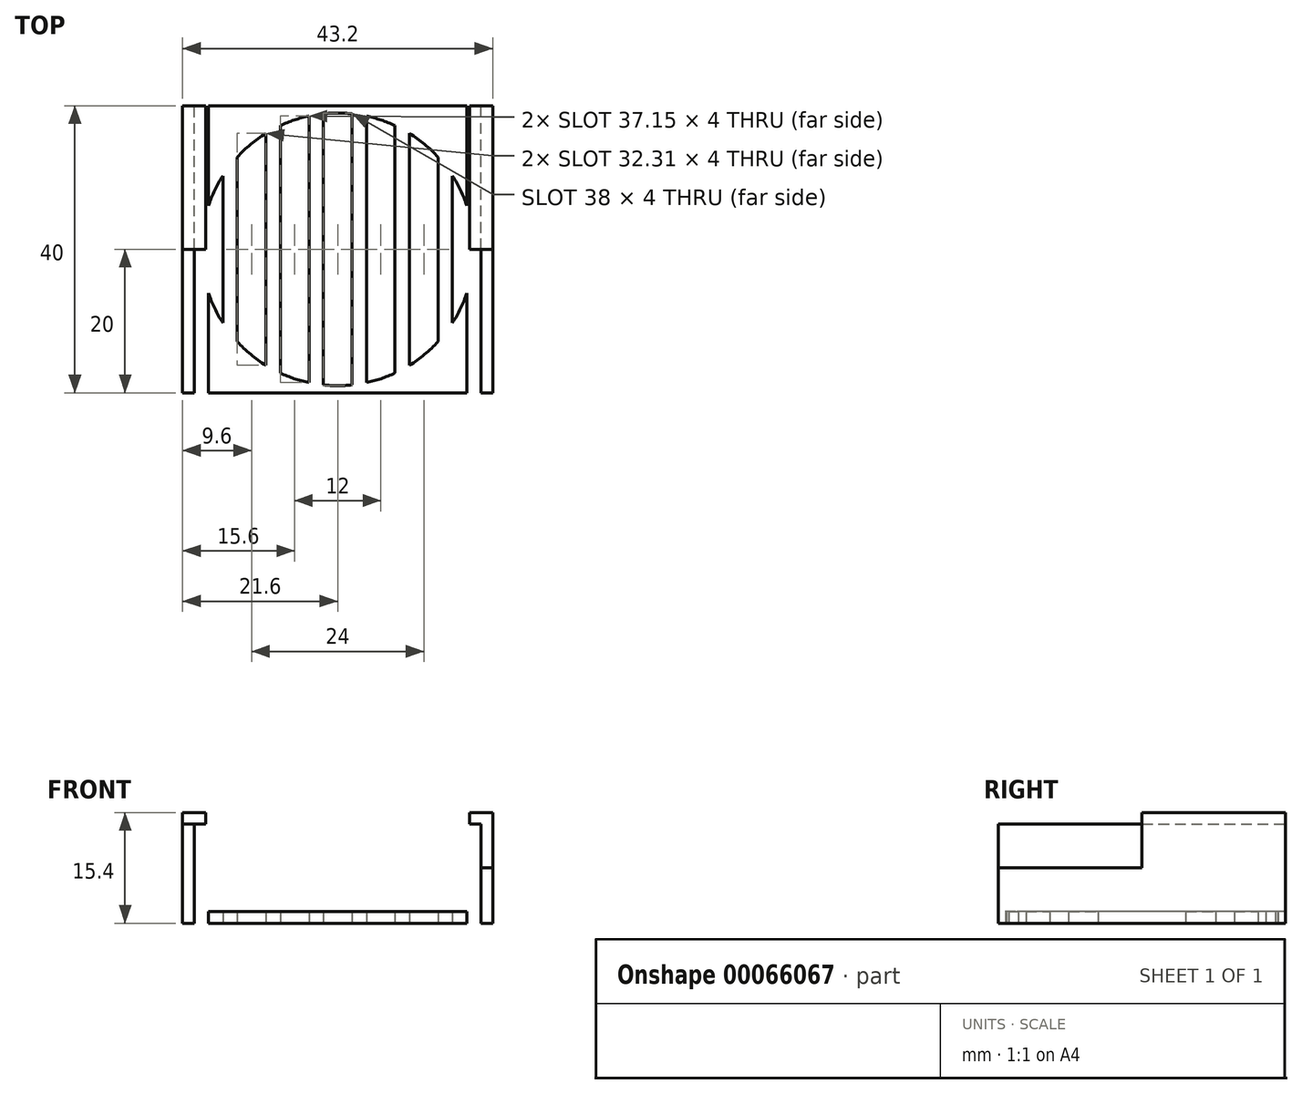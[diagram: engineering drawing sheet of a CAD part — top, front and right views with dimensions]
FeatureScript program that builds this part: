
annotation { "Feature Type Name" : "Feature", "Feature Type Description" : "" }
export const myFeature = defineFeature(function(context is Context, id is Id, definition is map)
    precondition{}
    {
        {
            var Q0;
            Q0=qCreatedBy(makeId("Top.planeOp"),FACE);
            var sketch = newSketch(context, id + "F0", { "sketchPlane" : qUnion([Q0])});
            skLineSegment(sketch, "E0.rect.bottom", {"start": v(20, -20) * mm, "end": v(-20, -20) * mm});
            skLineSegment(sketch, "E0.rect.top", {"start": v(20, 20) * mm, "end": v(-20, 20) * mm});
            skLineSegment(sketch, "E0.rect.left", {"start": v(20, -20) * mm, "end": v(20, 20) * mm});
            skLineSegment(sketch, "E0.rect.right", {"start": v(-20, -20) * mm, "end": v(-20, 20) * mm});
            skCircle(sketch, "E1", {"center": v(0, 0) * mm, "radius": 19 * mm});
            skLineSegment(sketch, "E2.bottom", {"start": v(-20, 20) * mm, "end": v(-21.6, 20) * mm});
            skLineSegment(sketch, "E2.top", {"start": v(-20, -20) * mm, "end": v(-21.6, -20) * mm});
            skLineSegment(sketch, "E2.left", {"start": v(-20, 20) * mm, "end": v(-20, -20) * mm});
            skLineSegment(sketch, "E2.right", {"start": v(-21.6, 20) * mm, "end": v(-21.6, -20) * mm});
            skLineSegment(sketch, "E3.bottom", {"start": v(20, 20) * mm, "end": v(21.6, 20) * mm});
            skLineSegment(sketch, "E3.top", {"start": v(20, -20) * mm, "end": v(21.6, -20) * mm});
            skLineSegment(sketch, "E3.left", {"start": v(20, 20) * mm, "end": v(20, -20) * mm});
            skLineSegment(sketch, "E3.right", {"start": v(21.6, 20) * mm, "end": v(21.6, -20) * mm});
            skLineSegment(sketch, "E4.bottom", {"start": v(-20, 20) * mm, "end": v(-20, 20) * mm});
            skLineSegment(sketch, "E4.top", {"start": v(-20, -20) * mm, "end": v(-20, -20) * mm});
            skLineSegment(sketch, "E5.1.0.0", {"start": v(-18, 20) * mm, "end": v(-18, -20) * mm});
            skLineSegment(sketch, "E5.2.0.0", {"start": v(-16, 20) * mm, "end": v(-16, -20) * mm});
            skLineSegment(sketch, "E5.3.0.0", {"start": v(-14, 20) * mm, "end": v(-14, -20) * mm});
            skLineSegment(sketch, "E5.4.0.0", {"start": v(-12, 20) * mm, "end": v(-12, -20) * mm});
            skLineSegment(sketch, "E5.5.0.0", {"start": v(-10, 20) * mm, "end": v(-10, -20) * mm});
            skLineSegment(sketch, "E5.6.0.0", {"start": v(-8, 20) * mm, "end": v(-8, -20) * mm});
            skLineSegment(sketch, "E5.7.0.0", {"start": v(-6, 20) * mm, "end": v(-6, -20) * mm});
            skLineSegment(sketch, "E5.8.0.0", {"start": v(-4, 20) * mm, "end": v(-4, -20) * mm});
            skLineSegment(sketch, "E5.9.0.0", {"start": v(-2, 20) * mm, "end": v(-2, -20) * mm});
            skLineSegment(sketch, "E5.10.0.0", {"start": v(0, 20) * mm, "end": v(0, -20) * mm});
            skLineSegment(sketch, "E5.11.0.0", {"start": v(2, 20) * mm, "end": v(2, -20) * mm});
            skLineSegment(sketch, "E5.12.0.0", {"start": v(4, 20) * mm, "end": v(4, -20) * mm});
            skLineSegment(sketch, "E5.13.0.0", {"start": v(6, 20) * mm, "end": v(6, -20) * mm});
            skLineSegment(sketch, "E5.direction1", {"start": v(-20, -20) * mm, "end": v(-18, -20) * mm, "construction": true});
            skLineSegment(sketch, "E6.0.14.0", {"start": v(8, 20) * mm, "end": v(8, -20) * mm});
            skLineSegment(sketch, "E6.0.15.0", {"start": v(10, 20) * mm, "end": v(10, -20) * mm});
            skLineSegment(sketch, "E6.0.16.0", {"start": v(12, 20) * mm, "end": v(12, -20) * mm});
            skLineSegment(sketch, "E6.0.17.0", {"start": v(14, 20) * mm, "end": v(14, -20) * mm});
            skLineSegment(sketch, "E6.0.18.0", {"start": v(16, 20) * mm, "end": v(16, -20) * mm});
            skLineSegment(sketch, "E6.0.19.0", {"start": v(18, 20) * mm, "end": v(18, -20) * mm});
            skSolve(sketch);
        }
        {
            var Q0;
            Q0=makeQuery(id+"F0.imprint","IMPRINT",FACE,{"disambiguationData":[TD([[makeQuery(id+"F0.imprint","IMPRINT",EDGE,{"derivedFrom":sQuery(id+"F0.wireOp",EDGE,"E2.bottom")}),1.0]])]});
            var Q1;
            Q1=makeQuery(id+"F0.imprint","IMPRINT",FACE,{"disambiguationData":[TD([[makeQuery(id+"F0.imprint","IMPRINT",EDGE,{"derivedFrom":sQuery(id+"F0.wireOp",EDGE,"E3.bottom")}),-1.0]])]});
            extrude(context, id + "F1", {"entities" : qUnion([Q0, Q1]), "depth" : (10.6 + 1.6) * mm});
        }
        {
            var Q0;
            {var subQ0=sQuery(id+"F0.wireOp",EDGE,"E5.12.0.0");var subQ1=sQuery(id+"F0.wireOp",EDGE,"E0.rect.bottom");var subQ2=makeQuery(id+"F0.imprint","INTERSECT",VERTEX,{"derivedFrom":[subQ1,subQ0]});Q0=makeQuery(id+"F0.imprint","IMPRINT",FACE,{"disambiguationData":[TD([[makeQuery(id+"F0.imprint","IMPRINT",EDGE,{"disambiguationData":[TD([[subQ2,1.0]])],"derivedFrom":subQ1}),-1.0]])]});}
            var Q1;
            {var subQ0=sQuery(id+"F0.wireOp",EDGE,"E5.12.0.0");var subQ1=sQuery(id+"F0.wireOp",EDGE,"E0.rect.top");var subQ2=makeQuery(id+"F0.imprint","INTERSECT",VERTEX,{"derivedFrom":[subQ1,subQ0]});Q1=makeQuery(id+"F0.imprint","IMPRINT",FACE,{"disambiguationData":[TD([[makeQuery(id+"F0.imprint","IMPRINT",EDGE,{"disambiguationData":[TD([[subQ2,1.0]])],"derivedFrom":subQ1}),1.0]])]});}
            var Q2;
            Q2=makeQuery(id+"F1.opExtrude","CAP_FACE",FACE,{"disambiguationData":[OSD([sQuery(id+"F0.wireOp",EDGE,"E2.bottom"),sQuery(id+"F0.wireOp",EDGE,"E2.top"),sQuery(id+"F0.wireOp",EDGE,"E2.right"),sQuery(id+"F0.wireOp",EDGE,"E2.left")])],"isStart":false});
            var Q3;
            {var subQ4=sQuery(id+"F0.wireOp",EDGE,"E2.left");Q3=makeQuery(id+"F0.imprint","IMPRINT",FACE,{"disambiguationData":[TD([[makeQuery(id+"F0.imprint","IMPRINT",EDGE,{"derivedFrom":subQ4}),1.0]])]});}
            var Q4;
            {var subQ0=sQuery(id+"F0.wireOp",EDGE,"E5.1.0.0");var subQ1=sQuery(id+"F0.wireOp",EDGE,"E0.rect.top");var subQ2=makeQuery(id+"F0.imprint","INTERSECT",VERTEX,{"derivedFrom":[subQ1,subQ0]});Q4=makeQuery(id+"F0.imprint","IMPRINT",FACE,{"disambiguationData":[TD([[makeQuery(id+"F0.imprint","IMPRINT",EDGE,{"disambiguationData":[TD([[subQ2,1.0]])],"derivedFrom":subQ1}),1.0]])]});}
            var Q5;
            {var subQ0=sQuery(id+"F0.wireOp",EDGE,"E5.2.0.0");var subQ1=sQuery(id+"F0.wireOp",EDGE,"E0.rect.top");var subQ2=makeQuery(id+"F0.imprint","INTERSECT",VERTEX,{"derivedFrom":[subQ1,subQ0]});Q5=makeQuery(id+"F0.imprint","IMPRINT",FACE,{"disambiguationData":[TD([[makeQuery(id+"F0.imprint","IMPRINT",EDGE,{"disambiguationData":[TD([[subQ2,1.0]])],"derivedFrom":subQ1}),1.0]])]});}
            var Q6;
            {var subQ0=sQuery(id+"F0.wireOp",EDGE,"E5.3.0.0");var subQ1=sQuery(id+"F0.wireOp",EDGE,"E0.rect.top");var subQ2=makeQuery(id+"F0.imprint","INTERSECT",VERTEX,{"derivedFrom":[subQ1,subQ0]});Q6=makeQuery(id+"F0.imprint","IMPRINT",FACE,{"disambiguationData":[TD([[makeQuery(id+"F0.imprint","IMPRINT",EDGE,{"disambiguationData":[TD([[subQ2,1.0]])],"derivedFrom":subQ1}),1.0]])]});}
            var Q7;
            {var subQ0=sQuery(id+"F0.wireOp",EDGE,"E5.4.0.0");var subQ1=sQuery(id+"F0.wireOp",EDGE,"E0.rect.top");var subQ2=makeQuery(id+"F0.imprint","INTERSECT",VERTEX,{"derivedFrom":[subQ1,subQ0]});Q7=makeQuery(id+"F0.imprint","IMPRINT",FACE,{"disambiguationData":[TD([[makeQuery(id+"F0.imprint","IMPRINT",EDGE,{"disambiguationData":[TD([[subQ2,1.0]])],"derivedFrom":subQ1}),1.0]])]});}
            var Q8;
            {var subQ0=sQuery(id+"F0.wireOp",EDGE,"E5.5.0.0");var subQ1=sQuery(id+"F0.wireOp",EDGE,"E0.rect.top");var subQ2=makeQuery(id+"F0.imprint","INTERSECT",VERTEX,{"derivedFrom":[subQ1,subQ0]});Q8=makeQuery(id+"F0.imprint","IMPRINT",FACE,{"disambiguationData":[TD([[makeQuery(id+"F0.imprint","IMPRINT",EDGE,{"disambiguationData":[TD([[subQ2,1.0]])],"derivedFrom":subQ1}),1.0]])]});}
            var Q9;
            {var subQ0=sQuery(id+"F0.wireOp",EDGE,"E5.6.0.0");var subQ1=sQuery(id+"F0.wireOp",EDGE,"E0.rect.top");var subQ2=makeQuery(id+"F0.imprint","INTERSECT",VERTEX,{"derivedFrom":[subQ1,subQ0]});Q9=makeQuery(id+"F0.imprint","IMPRINT",FACE,{"disambiguationData":[TD([[makeQuery(id+"F0.imprint","IMPRINT",EDGE,{"disambiguationData":[TD([[subQ2,1.0]])],"derivedFrom":subQ1}),1.0]])]});}
            var Q10;
            {var subQ0=sQuery(id+"F0.wireOp",EDGE,"E5.7.0.0");var subQ1=sQuery(id+"F0.wireOp",EDGE,"E0.rect.top");var subQ2=makeQuery(id+"F0.imprint","INTERSECT",VERTEX,{"derivedFrom":[subQ1,subQ0]});Q10=makeQuery(id+"F0.imprint","IMPRINT",FACE,{"disambiguationData":[TD([[makeQuery(id+"F0.imprint","IMPRINT",EDGE,{"disambiguationData":[TD([[subQ2,1.0]])],"derivedFrom":subQ1}),1.0]])]});}
            var Q11;
            {var subQ0=sQuery(id+"F0.wireOp",EDGE,"E5.8.0.0");var subQ1=sQuery(id+"F0.wireOp",EDGE,"E0.rect.top");var subQ2=makeQuery(id+"F0.imprint","INTERSECT",VERTEX,{"derivedFrom":[subQ1,subQ0]});Q11=makeQuery(id+"F0.imprint","IMPRINT",FACE,{"disambiguationData":[TD([[makeQuery(id+"F0.imprint","IMPRINT",EDGE,{"disambiguationData":[TD([[subQ2,1.0]])],"derivedFrom":subQ1}),1.0]])]});}
            var Q12;
            {var subQ0=sQuery(id+"F0.wireOp",EDGE,"E5.9.0.0");var subQ1=sQuery(id+"F0.wireOp",EDGE,"E0.rect.top");var subQ2=makeQuery(id+"F0.imprint","INTERSECT",VERTEX,{"derivedFrom":[subQ1,subQ0]});Q12=makeQuery(id+"F0.imprint","IMPRINT",FACE,{"disambiguationData":[TD([[makeQuery(id+"F0.imprint","IMPRINT",EDGE,{"disambiguationData":[TD([[subQ2,1.0]])],"derivedFrom":subQ1}),1.0]])]});}
            var Q13;
            {var subQ0=sQuery(id+"F0.wireOp",EDGE,"E5.10.0.0");var subQ1=sQuery(id+"F0.wireOp",EDGE,"E0.rect.top");var subQ2=makeQuery(id+"F0.imprint","INTERSECT",VERTEX,{"derivedFrom":[subQ1,subQ0]});Q13=makeQuery(id+"F0.imprint","IMPRINT",FACE,{"disambiguationData":[TD([[makeQuery(id+"F0.imprint","IMPRINT",EDGE,{"disambiguationData":[TD([[subQ2,1.0]])],"derivedFrom":subQ1}),1.0]])]});}
            var Q14;
            {var subQ0=sQuery(id+"F0.wireOp",EDGE,"E5.11.0.0");var subQ1=sQuery(id+"F0.wireOp",EDGE,"E0.rect.top");var subQ2=makeQuery(id+"F0.imprint","INTERSECT",VERTEX,{"derivedFrom":[subQ1,subQ0]});Q14=makeQuery(id+"F0.imprint","IMPRINT",FACE,{"disambiguationData":[TD([[makeQuery(id+"F0.imprint","IMPRINT",EDGE,{"disambiguationData":[TD([[subQ2,1.0]])],"derivedFrom":subQ1}),1.0]])]});}
            var Q15;
            Q15=makeQuery(id+"F1.opExtrude","CAP_FACE",FACE,{"disambiguationData":[OSD([sQuery(id+"F0.wireOp",EDGE,"E3.bottom"),sQuery(id+"F0.wireOp",EDGE,"E3.top"),sQuery(id+"F0.wireOp",EDGE,"E3.right"),sQuery(id+"F0.wireOp",EDGE,"E3.left")])],"isStart":false});
            var Q16;
            {var subQ0=sQuery(id+"F0.wireOp",EDGE,"E5.11.0.0");var subQ1=sQuery(id+"F0.wireOp",EDGE,"E0.rect.bottom");var subQ2=makeQuery(id+"F0.imprint","INTERSECT",VERTEX,{"derivedFrom":[subQ1,subQ0]});Q16=makeQuery(id+"F0.imprint","IMPRINT",FACE,{"disambiguationData":[TD([[makeQuery(id+"F0.imprint","IMPRINT",EDGE,{"disambiguationData":[TD([[subQ2,1.0]])],"derivedFrom":subQ1}),-1.0]])]});}
            var Q17;
            {var subQ0=sQuery(id+"F0.wireOp",EDGE,"E5.10.0.0");var subQ1=sQuery(id+"F0.wireOp",EDGE,"E0.rect.bottom");var subQ2=makeQuery(id+"F0.imprint","INTERSECT",VERTEX,{"derivedFrom":[subQ1,subQ0]});Q17=makeQuery(id+"F0.imprint","IMPRINT",FACE,{"disambiguationData":[TD([[makeQuery(id+"F0.imprint","IMPRINT",EDGE,{"disambiguationData":[TD([[subQ2,1.0]])],"derivedFrom":subQ1}),-1.0]])]});}
            var Q18;
            {var subQ0=sQuery(id+"F0.wireOp",EDGE,"E5.9.0.0");var subQ1=sQuery(id+"F0.wireOp",EDGE,"E0.rect.bottom");var subQ2=makeQuery(id+"F0.imprint","INTERSECT",VERTEX,{"derivedFrom":[subQ1,subQ0]});Q18=makeQuery(id+"F0.imprint","IMPRINT",FACE,{"disambiguationData":[TD([[makeQuery(id+"F0.imprint","IMPRINT",EDGE,{"disambiguationData":[TD([[subQ2,1.0]])],"derivedFrom":subQ1}),-1.0]])]});}
            var Q19;
            {var subQ0=sQuery(id+"F0.wireOp",EDGE,"E5.8.0.0");var subQ1=sQuery(id+"F0.wireOp",EDGE,"E0.rect.bottom");var subQ2=makeQuery(id+"F0.imprint","INTERSECT",VERTEX,{"derivedFrom":[subQ1,subQ0]});Q19=makeQuery(id+"F0.imprint","IMPRINT",FACE,{"disambiguationData":[TD([[makeQuery(id+"F0.imprint","IMPRINT",EDGE,{"disambiguationData":[TD([[subQ2,1.0]])],"derivedFrom":subQ1}),-1.0]])]});}
            var Q20;
            {var subQ0=sQuery(id+"F0.wireOp",EDGE,"E5.7.0.0");var subQ1=sQuery(id+"F0.wireOp",EDGE,"E0.rect.bottom");var subQ2=makeQuery(id+"F0.imprint","INTERSECT",VERTEX,{"derivedFrom":[subQ1,subQ0]});Q20=makeQuery(id+"F0.imprint","IMPRINT",FACE,{"disambiguationData":[TD([[makeQuery(id+"F0.imprint","IMPRINT",EDGE,{"disambiguationData":[TD([[subQ2,1.0]])],"derivedFrom":subQ1}),-1.0]])]});}
            var Q21;
            {var subQ0=sQuery(id+"F0.wireOp",EDGE,"E5.6.0.0");var subQ1=sQuery(id+"F0.wireOp",EDGE,"E0.rect.bottom");var subQ2=makeQuery(id+"F0.imprint","INTERSECT",VERTEX,{"derivedFrom":[subQ1,subQ0]});Q21=makeQuery(id+"F0.imprint","IMPRINT",FACE,{"disambiguationData":[TD([[makeQuery(id+"F0.imprint","IMPRINT",EDGE,{"disambiguationData":[TD([[subQ2,1.0]])],"derivedFrom":subQ1}),-1.0]])]});}
            var Q22;
            {var subQ0=sQuery(id+"F0.wireOp",EDGE,"E5.5.0.0");var subQ1=sQuery(id+"F0.wireOp",EDGE,"E0.rect.bottom");var subQ2=makeQuery(id+"F0.imprint","INTERSECT",VERTEX,{"derivedFrom":[subQ1,subQ0]});Q22=makeQuery(id+"F0.imprint","IMPRINT",FACE,{"disambiguationData":[TD([[makeQuery(id+"F0.imprint","IMPRINT",EDGE,{"disambiguationData":[TD([[subQ2,1.0]])],"derivedFrom":subQ1}),-1.0]])]});}
            var Q23;
            {var subQ0=sQuery(id+"F0.wireOp",EDGE,"E5.4.0.0");var subQ1=sQuery(id+"F0.wireOp",EDGE,"E0.rect.bottom");var subQ2=makeQuery(id+"F0.imprint","INTERSECT",VERTEX,{"derivedFrom":[subQ1,subQ0]});Q23=makeQuery(id+"F0.imprint","IMPRINT",FACE,{"disambiguationData":[TD([[makeQuery(id+"F0.imprint","IMPRINT",EDGE,{"disambiguationData":[TD([[subQ2,1.0]])],"derivedFrom":subQ1}),-1.0]])]});}
            var Q24;
            {var subQ0=sQuery(id+"F0.wireOp",EDGE,"E5.3.0.0");var subQ1=sQuery(id+"F0.wireOp",EDGE,"E0.rect.bottom");var subQ2=makeQuery(id+"F0.imprint","INTERSECT",VERTEX,{"derivedFrom":[subQ1,subQ0]});Q24=makeQuery(id+"F0.imprint","IMPRINT",FACE,{"disambiguationData":[TD([[makeQuery(id+"F0.imprint","IMPRINT",EDGE,{"disambiguationData":[TD([[subQ2,1.0]])],"derivedFrom":subQ1}),-1.0]])]});}
            var Q25;
            {var subQ0=sQuery(id+"F0.wireOp",EDGE,"E5.2.0.0");var subQ1=sQuery(id+"F0.wireOp",EDGE,"E0.rect.bottom");var subQ2=makeQuery(id+"F0.imprint","INTERSECT",VERTEX,{"derivedFrom":[subQ1,subQ0]});Q25=makeQuery(id+"F0.imprint","IMPRINT",FACE,{"disambiguationData":[TD([[makeQuery(id+"F0.imprint","IMPRINT",EDGE,{"disambiguationData":[TD([[subQ2,1.0]])],"derivedFrom":subQ1}),-1.0]])]});}
            var Q26;
            {var subQ0=sQuery(id+"F0.wireOp",EDGE,"E5.1.0.0");var subQ1=sQuery(id+"F0.wireOp",EDGE,"E0.rect.bottom");var subQ2=makeQuery(id+"F0.imprint","INTERSECT",VERTEX,{"derivedFrom":[subQ1,subQ0]});Q26=makeQuery(id+"F0.imprint","IMPRINT",FACE,{"disambiguationData":[TD([[makeQuery(id+"F0.imprint","IMPRINT",EDGE,{"disambiguationData":[TD([[subQ2,1.0]])],"derivedFrom":subQ1}),-1.0]])]});}
            var Q27;
            {var subQ0=sQuery(id+"F0.wireOp",EDGE,"E5.13.0.0");var subQ1=sQuery(id+"F0.wireOp",EDGE,"E0.rect.bottom");var subQ2=makeQuery(id+"F0.imprint","INTERSECT",VERTEX,{"derivedFrom":[subQ1,subQ0]});Q27=makeQuery(id+"F0.imprint","IMPRINT",FACE,{"disambiguationData":[TD([[makeQuery(id+"F0.imprint","IMPRINT",EDGE,{"disambiguationData":[TD([[subQ2,1.0]])],"derivedFrom":subQ1}),-1.0]])]});}
            var Q28;
            {var subQ0=sQuery(id+"F0.wireOp",EDGE,"E6.0.14.0");var subQ1=sQuery(id+"F0.wireOp",EDGE,"E0.rect.bottom");var subQ2=makeQuery(id+"F0.imprint","INTERSECT",VERTEX,{"derivedFrom":[subQ1,subQ0]});Q28=makeQuery(id+"F0.imprint","IMPRINT",FACE,{"disambiguationData":[TD([[makeQuery(id+"F0.imprint","IMPRINT",EDGE,{"disambiguationData":[TD([[subQ2,1.0]])],"derivedFrom":subQ1}),-1.0]])]});}
            var Q29;
            {var subQ0=sQuery(id+"F0.wireOp",EDGE,"E6.0.15.0");var subQ1=sQuery(id+"F0.wireOp",EDGE,"E0.rect.bottom");var subQ2=makeQuery(id+"F0.imprint","INTERSECT",VERTEX,{"derivedFrom":[subQ1,subQ0]});Q29=makeQuery(id+"F0.imprint","IMPRINT",FACE,{"disambiguationData":[TD([[makeQuery(id+"F0.imprint","IMPRINT",EDGE,{"disambiguationData":[TD([[subQ2,1.0]])],"derivedFrom":subQ1}),-1.0]])]});}
            var Q30;
            {var subQ0=sQuery(id+"F0.wireOp",EDGE,"E6.0.16.0");var subQ1=sQuery(id+"F0.wireOp",EDGE,"E0.rect.bottom");var subQ2=makeQuery(id+"F0.imprint","INTERSECT",VERTEX,{"derivedFrom":[subQ1,subQ0]});Q30=makeQuery(id+"F0.imprint","IMPRINT",FACE,{"disambiguationData":[TD([[makeQuery(id+"F0.imprint","IMPRINT",EDGE,{"disambiguationData":[TD([[subQ2,1.0]])],"derivedFrom":subQ1}),-1.0]])]});}
            var Q31;
            {var subQ0=sQuery(id+"F0.wireOp",EDGE,"E6.0.17.0");var subQ1=sQuery(id+"F0.wireOp",EDGE,"E0.rect.bottom");var subQ2=makeQuery(id+"F0.imprint","INTERSECT",VERTEX,{"derivedFrom":[subQ1,subQ0]});Q31=makeQuery(id+"F0.imprint","IMPRINT",FACE,{"disambiguationData":[TD([[makeQuery(id+"F0.imprint","IMPRINT",EDGE,{"disambiguationData":[TD([[subQ2,1.0]])],"derivedFrom":subQ1}),-1.0]])]});}
            var Q32;
            {var subQ0=sQuery(id+"F0.wireOp",EDGE,"E6.0.18.0");var subQ1=sQuery(id+"F0.wireOp",EDGE,"E0.rect.bottom");var subQ2=makeQuery(id+"F0.imprint","INTERSECT",VERTEX,{"derivedFrom":[subQ1,subQ0]});Q32=makeQuery(id+"F0.imprint","IMPRINT",FACE,{"disambiguationData":[TD([[makeQuery(id+"F0.imprint","IMPRINT",EDGE,{"disambiguationData":[TD([[subQ2,1.0]])],"derivedFrom":subQ1}),-1.0]])]});}
            var Q33;
            {var subQ6=sQuery(id+"F0.wireOp",EDGE,"E3.left");Q33=makeQuery(id+"F0.imprint","IMPRINT",FACE,{"disambiguationData":[TD([[makeQuery(id+"F0.imprint","IMPRINT",EDGE,{"derivedFrom":subQ6}),-1.0]])]});}
            var Q34;
            Q34=makeQuery(id+"F0.imprint","IMPRINT",FACE,{"disambiguationData":[TD([[makeQuery(id+"F0.imprint","IMPRINT",EDGE,{"derivedFrom":sQuery(id+"F0.wireOp",EDGE,"E3.bottom")}),-1.0]])]});
            var Q35;
            {var subQ0=sQuery(id+"F0.wireOp",EDGE,"E6.0.18.0");var subQ1=sQuery(id+"F0.wireOp",EDGE,"E0.rect.top");var subQ2=makeQuery(id+"F0.imprint","INTERSECT",VERTEX,{"derivedFrom":[subQ1,subQ0]});Q35=makeQuery(id+"F0.imprint","IMPRINT",FACE,{"disambiguationData":[TD([[makeQuery(id+"F0.imprint","IMPRINT",EDGE,{"disambiguationData":[TD([[subQ2,1.0]])],"derivedFrom":subQ1}),1.0]])]});}
            var Q36;
            {var subQ0=sQuery(id+"F0.wireOp",EDGE,"E6.0.17.0");var subQ1=sQuery(id+"F0.wireOp",EDGE,"E0.rect.top");var subQ2=makeQuery(id+"F0.imprint","INTERSECT",VERTEX,{"derivedFrom":[subQ1,subQ0]});Q36=makeQuery(id+"F0.imprint","IMPRINT",FACE,{"disambiguationData":[TD([[makeQuery(id+"F0.imprint","IMPRINT",EDGE,{"disambiguationData":[TD([[subQ2,1.0]])],"derivedFrom":subQ1}),1.0]])]});}
            var Q37;
            {var subQ0=sQuery(id+"F0.wireOp",EDGE,"E6.0.16.0");var subQ1=sQuery(id+"F0.wireOp",EDGE,"E0.rect.top");var subQ2=makeQuery(id+"F0.imprint","INTERSECT",VERTEX,{"derivedFrom":[subQ1,subQ0]});Q37=makeQuery(id+"F0.imprint","IMPRINT",FACE,{"disambiguationData":[TD([[makeQuery(id+"F0.imprint","IMPRINT",EDGE,{"disambiguationData":[TD([[subQ2,1.0]])],"derivedFrom":subQ1}),1.0]])]});}
            var Q38;
            {var subQ0=sQuery(id+"F0.wireOp",EDGE,"E6.0.15.0");var subQ1=sQuery(id+"F0.wireOp",EDGE,"E0.rect.top");var subQ2=makeQuery(id+"F0.imprint","INTERSECT",VERTEX,{"derivedFrom":[subQ1,subQ0]});Q38=makeQuery(id+"F0.imprint","IMPRINT",FACE,{"disambiguationData":[TD([[makeQuery(id+"F0.imprint","IMPRINT",EDGE,{"disambiguationData":[TD([[subQ2,1.0]])],"derivedFrom":subQ1}),1.0]])]});}
            var Q39;
            {var subQ0=sQuery(id+"F0.wireOp",EDGE,"E6.0.14.0");var subQ1=sQuery(id+"F0.wireOp",EDGE,"E0.rect.top");var subQ2=makeQuery(id+"F0.imprint","INTERSECT",VERTEX,{"derivedFrom":[subQ1,subQ0]});Q39=makeQuery(id+"F0.imprint","IMPRINT",FACE,{"disambiguationData":[TD([[makeQuery(id+"F0.imprint","IMPRINT",EDGE,{"disambiguationData":[TD([[subQ2,1.0]])],"derivedFrom":subQ1}),1.0]])]});}
            var Q40;
            {var subQ0=sQuery(id+"F0.wireOp",EDGE,"E5.13.0.0");var subQ1=sQuery(id+"F0.wireOp",EDGE,"E0.rect.top");var subQ2=makeQuery(id+"F0.imprint","INTERSECT",VERTEX,{"derivedFrom":[subQ1,subQ0]});Q40=makeQuery(id+"F0.imprint","IMPRINT",FACE,{"disambiguationData":[TD([[makeQuery(id+"F0.imprint","IMPRINT",EDGE,{"disambiguationData":[TD([[subQ2,1.0]])],"derivedFrom":subQ1}),1.0]])]});}
            var Q41;
            {var subQ0=sQuery(id+"F0.wireOp",EDGE,"E5.3.0.0");var subQ1=sQuery(id+"F0.wireOp",EDGE,"E1");var subQ2=makeQuery(id+"F0.imprint","INTERSECT",VERTEX,{"disambiguationData":[OD(0.0)],"derivedFrom":[subQ1,subQ0]});Q41=makeQuery(id+"F0.imprint","IMPRINT",FACE,{"disambiguationData":[TD([[makeQuery(id+"F0.imprint","IMPRINT",EDGE,{"disambiguationData":[TD([[subQ2,-1.0]])],"derivedFrom":subQ1}),1.0]])]});}
            var Q42;
            {var subQ0=sQuery(id+"F0.wireOp",EDGE,"E5.6.0.0");var subQ1=sQuery(id+"F0.wireOp",EDGE,"E1");var subQ2=makeQuery(id+"F0.imprint","INTERSECT",VERTEX,{"disambiguationData":[OD(0.0)],"derivedFrom":[subQ1,subQ0]});Q42=makeQuery(id+"F0.imprint","IMPRINT",FACE,{"disambiguationData":[TD([[makeQuery(id+"F0.imprint","IMPRINT",EDGE,{"disambiguationData":[TD([[subQ2,-1.0]])],"derivedFrom":subQ1}),1.0]])]});}
            var Q43;
            {var subQ0=sQuery(id+"F0.wireOp",EDGE,"E5.9.0.0");var subQ1=sQuery(id+"F0.wireOp",EDGE,"E1");var subQ2=makeQuery(id+"F0.imprint","INTERSECT",VERTEX,{"disambiguationData":[OD(0.0)],"derivedFrom":[subQ1,subQ0]});Q43=makeQuery(id+"F0.imprint","IMPRINT",FACE,{"disambiguationData":[TD([[makeQuery(id+"F0.imprint","IMPRINT",EDGE,{"disambiguationData":[TD([[subQ2,-1.0]])],"derivedFrom":subQ1}),1.0]])]});}
            var Q44;
            {var subQ0=sQuery(id+"F0.wireOp",EDGE,"E5.12.0.0");var subQ1=sQuery(id+"F0.wireOp",EDGE,"E1");var subQ2=makeQuery(id+"F0.imprint","INTERSECT",VERTEX,{"disambiguationData":[OD(0.0)],"derivedFrom":[subQ1,subQ0]});Q44=makeQuery(id+"F0.imprint","IMPRINT",FACE,{"disambiguationData":[TD([[makeQuery(id+"F0.imprint","IMPRINT",EDGE,{"disambiguationData":[TD([[subQ2,-1.0]])],"derivedFrom":subQ1}),1.0]])]});}
            var Q45;
            {var subQ0=sQuery(id+"F0.wireOp",EDGE,"E6.0.15.0");var subQ1=sQuery(id+"F0.wireOp",EDGE,"E1");var subQ2=makeQuery(id+"F0.imprint","INTERSECT",VERTEX,{"disambiguationData":[OD(0.0)],"derivedFrom":[subQ1,subQ0]});Q45=makeQuery(id+"F0.imprint","IMPRINT",FACE,{"disambiguationData":[TD([[makeQuery(id+"F0.imprint","IMPRINT",EDGE,{"disambiguationData":[TD([[subQ2,-1.0]])],"derivedFrom":subQ1}),1.0]])]});}
            var Q46;
            {var subQ0=sQuery(id+"F0.wireOp",EDGE,"E6.0.18.0");var subQ1=sQuery(id+"F0.wireOp",EDGE,"E1");var subQ2=makeQuery(id+"F0.imprint","INTERSECT",VERTEX,{"disambiguationData":[OD(0.0)],"derivedFrom":[subQ1,subQ0]});Q46=makeQuery(id+"F0.imprint","IMPRINT",FACE,{"disambiguationData":[TD([[makeQuery(id+"F0.imprint","IMPRINT",EDGE,{"disambiguationData":[TD([[subQ2,-1.0]])],"derivedFrom":subQ1}),1.0]])]});}
            extrude(context, id + "F2", {"entities" : qUnion([Q0, Q1, Q2, Q3, Q4, Q5, Q6, Q7, Q8, Q9, Q10, Q11, Q12, Q13, Q14, Q15, Q16, Q17, Q18, Q19, Q20, Q21, Q22, Q23, Q24, Q25, Q26, Q27, Q28, Q29, Q30, Q31, Q32, Q33, Q34, Q35, Q36, Q37, Q38, Q39, Q40, Q41, Q42, Q43, Q44, Q45, Q46]), "operationType" : NewBodyOperationType.ADD, "depth" : 1.6 * mm});
        }
        {
            var Q0;
            Q0=makeQuery(id+"F2.opExtrude","CAP_FACE",FACE,{"disambiguationData":[OSD([sQuery(id+"F0.wireOp",EDGE,"E2.bottom"),sQuery(id+"F0.wireOp",EDGE,"E2.top"),sQuery(id+"F0.wireOp",EDGE,"E2.right"),sQuery(id+"F0.wireOp",EDGE,"E2.left")])],"isStart":false});
            var sketch = newSketch(context, id + "F3", { "sketchPlane" : qUnion([Q0])});
            skLineSegment(sketch, "E7.bottom", {"start": v(-21.6, 20) * mm, "end": v(-18.4, 20) * mm});
            skLineSegment(sketch, "E7.top", {"start": v(-21.6, -20) * mm, "end": v(-18.4, -20) * mm});
            skLineSegment(sketch, "E7.left", {"start": v(-21.6, 20) * mm, "end": v(-21.6, -20) * mm});
            skLineSegment(sketch, "E7.right", {"start": v(-18.4, 20) * mm, "end": v(-18.4, -20) * mm});
            skLineSegment(sketch, "E8.bottom", {"start": v(21.6, 20) * mm, "end": v(18.4, 20) * mm});
            skLineSegment(sketch, "E8.top", {"start": v(21.6, -20) * mm, "end": v(18.4, -20) * mm});
            skLineSegment(sketch, "E8.left", {"start": v(21.6, 20) * mm, "end": v(21.6, -20) * mm});
            skLineSegment(sketch, "E8.right", {"start": v(18.4, 20) * mm, "end": v(18.4, -20) * mm});
            skLineSegment(sketch, "E9", {"start": v(-21.6, 0) * mm, "end": v(-18.4, 0) * mm});
            skLineSegment(sketch, "E10", {"start": v(21.6, 0) * mm, "end": v(18.4, 0) * mm});
            skPoint(sketch, "E11.0", {"position": v(21.6, 20) * mm});
            skPoint(sketch, "E12.0", {"position": v(20, -20) * mm});
            skSolve(sketch);
        }
        {
            var Q0;
            {var subQ0=sQuery(id+"F3.wireOp",EDGE,"E8.bottom");Q0=makeQuery(id+"F3.imprint","IMPRINT",FACE,{"disambiguationData":[TD([[makeQuery(id+"F3.imprint","IMPRINT",EDGE,{"derivedFrom":subQ0}),1.0]])]});}
            var Q1;
            {var subQ0=sQuery(id+"F3.wireOp",EDGE,"E7.bottom");var subQ3=sQuery(id+"F3.wireOp",EDGE,"E7.left");var subQ4=makeQuery(id+"F3.imprint","INTERSECT",VERTEX,{"derivedFrom":[subQ0,subQ3]});Q1=makeQuery(id+"F3.imprint","IMPRINT",FACE,{"disambiguationData":[TD([[makeQuery(id+"F3.imprint","IMPRINT",EDGE,{"disambiguationData":[TD([[subQ4,1.0]])],"derivedFrom":subQ0}),1.0]])]});}
            var Q2;
            {var subQ0=sQuery(id+"F3.wireOp",EDGE,"E7.bottom");var subQ3=sQuery(id+"F3.wireOp",EDGE,"E7.right");var subQ4=makeQuery(id+"F3.imprint","INTERSECT",VERTEX,{"derivedFrom":[subQ0,subQ3]});Q2=makeQuery(id+"F3.imprint","IMPRINT",FACE,{"disambiguationData":[TD([[makeQuery(id+"F3.imprint","IMPRINT",EDGE,{"disambiguationData":[TD([[subQ4,1.0]])],"derivedFrom":subQ0}),-1.0]])]});}
            extrude(context, id + "F4", {"entities" : qUnion([Q0, Q1, Q2]), "operationType" : NewBodyOperationType.ADD, "depth" : 1.6 * mm});
        }
        {
            var Q0;
            Q0=makeQuery(id+"F2.opExtrude","CAP_FACE",FACE,{"disambiguationData":[OSD([sQuery(id+"F0.wireOp",EDGE,"E3.bottom"),sQuery(id+"F0.wireOp",EDGE,"E3.top"),sQuery(id+"F0.wireOp",EDGE,"E3.right"),sQuery(id+"F0.wireOp",EDGE,"E3.left")])],"isStart":false});
            extrude(context, id + "F5", {"entities" : qUnion([Q0]), "operationType" : NewBodyOperationType.REMOVE, "oppositeDirection" : true, "depth" : (12.2 / 2) * mm});
        }
    });
